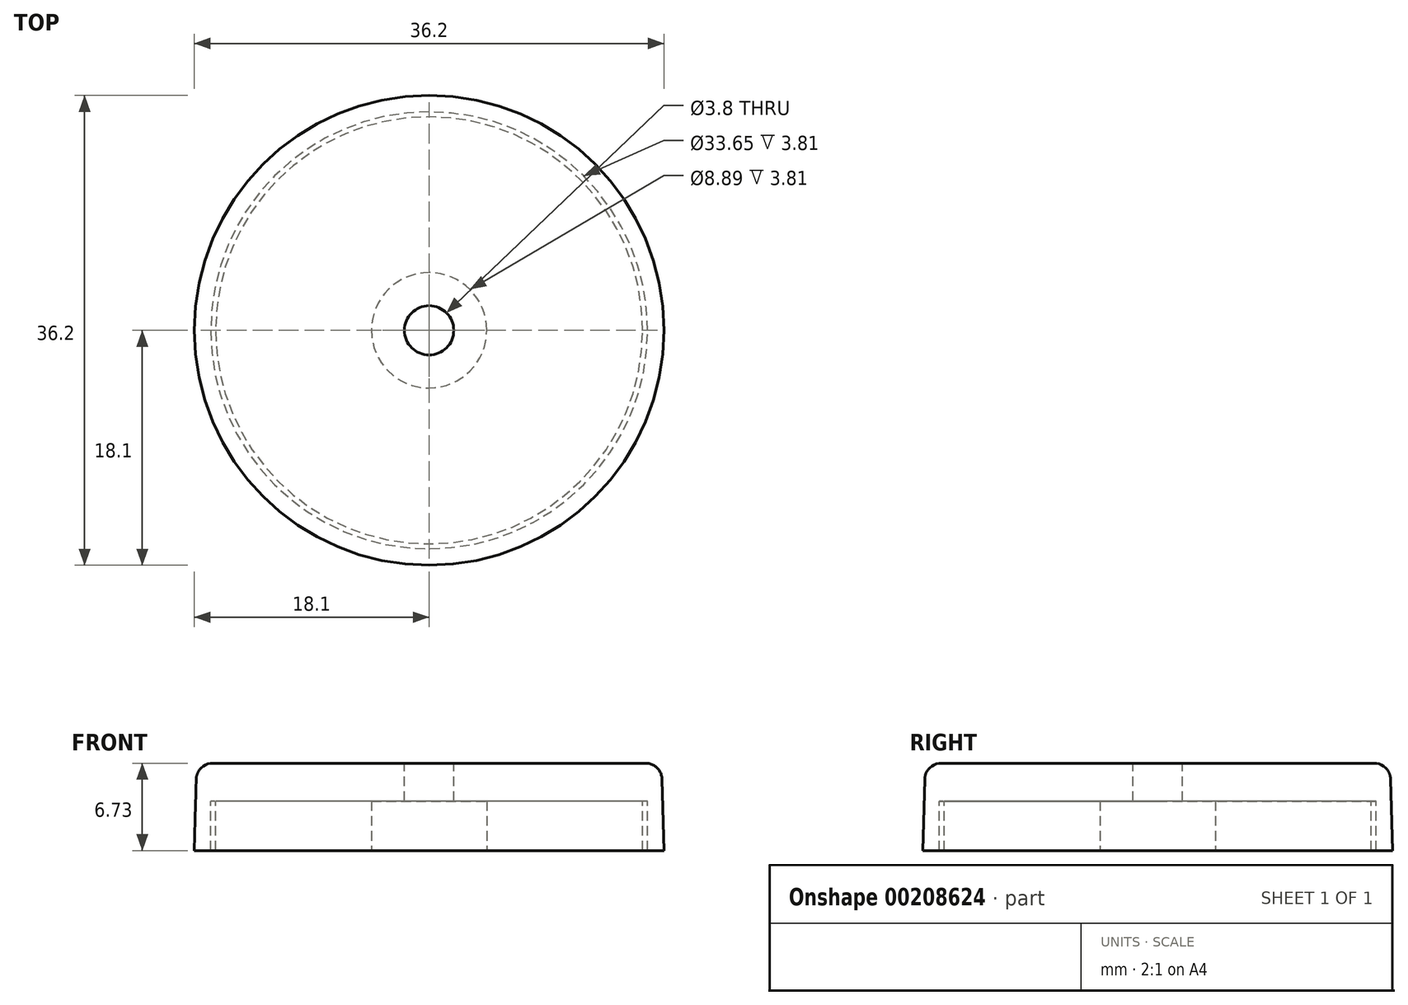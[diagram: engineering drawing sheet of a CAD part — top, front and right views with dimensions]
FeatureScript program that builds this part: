
annotation { "Feature Type Name" : "Feature", "Feature Type Description" : "" }
export const myFeature = defineFeature(function(context is Context, id is Id, definition is map)
    precondition{}
    {
        {
            var Q0;
            Q0=qCreatedBy(makeId("Front.planeOp"),FACE);
            var sketch = newSketch(context, id + "F0", { "sketchPlane" : qUnion([Q0])});
            skLineSegment(sketch, "E0.bottom", {"start": v(0, 6.73) * mm, "end": v(18.1, 6.73) * mm});
            skLineSegment(sketch, "E0.top", {"start": v(0, 0) * mm, "end": v(18.1, 0) * mm});
            skLineSegment(sketch, "E0.left", {"start": v(0, 6.73) * mm, "end": v(0, 0) * mm});
            skLineSegment(sketch, "E0.right", {"start": v(18.1, 6.73) * mm, "end": v(18.1, 0) * mm});
            skLineSegment(sketch, "E1", {"start": v(18.1, 0) * mm, "end": v(17.91, 6.73) * mm});
            skLineSegment(sketch, "E2.bottom", {"start": v(16.83, 0) * mm, "end": v(16.45, 0) * mm});
            skLineSegment(sketch, "E2.top", {"start": v(16.83, 3.8) * mm, "end": v(16.45, 3.8) * mm});
            skLineSegment(sketch, "E2.left", {"start": v(16.83, 0) * mm, "end": v(16.83, 3.81) * mm});
            skLineSegment(sketch, "E2.right", {"start": v(16.45, 0) * mm, "end": v(16.45, 3.81) * mm});
            skSolve(sketch);
        }
        {
            var Q0;
            Q0=makeQuery(id+"F0.imprint","IMPRINT",FACE,{"disambiguationData":[TD([[makeQuery(id+"F0.imprint","IMPRINT",EDGE,{"derivedFrom":sQuery(id+"F0.wireOp",EDGE,"E0.top")}),1.0]])]});
            var Q1;
            Q1=sQuery(id+"F0.wireOp",EDGE,"E0.left");
            revolve(context, id + "F1", {"entities" : qUnion([Q0]), "axis" : qUnion([Q1]), "revolveType" : RevolveType.FULL});
        }
        {
            var Q0;
            Q0=makeQuery(id+"F1.opRevolve","SWEPT_FACE",FACE,{"disambiguationData":[OSD([sQuery(id+"F0.wireOp",EDGE,"E0.bottom")])]});
            var sketch = newSketch(context, id + "F2", { "sketchPlane" : qUnion([Q0])});
            skPoint(sketch, "E3", {"position": v(0, 0) * mm});
            skSolve(sketch);
        }
        {
            var Q0;
            Q0=sQuery(id+"F2.wireOp",VERTEX,"E3");
            var Q1;
            Q1=makeQuery(id+"F1.opRevolve","SWEPT_BODY",BODY,{"disambiguationData":[OSD([sQuery(id+"F0.wireOp",EDGE,"E0.bottom"),sQuery(id+"F0.wireOp",EDGE,"E0.top"),sQuery(id+"F0.wireOp",EDGE,"E0.left"),sQuery(id+"F0.wireOp",EDGE,"E1")])]});
            hole(context, id + "F3", {"style" : HoleStyle.SIMPLE, "endStyle" : HoleEndStyle.THROUGH, "standardTappedOrClearance" : lookupTablePath({ "standard" : "ANSI", "fit" : "Normal (ASME)", "size" : "#6", "type" : "Clearance" }), "standardBlindInLast" : lookupTablePath({ "fit" : "Free", "standard" : "ANSI", "size" : "#6", "type" : "Clearance" }), "holeDiameter" : 3.8 * mm, "locations" : qUnion([Q0]), "scope" : qUnion([Q1]), "isTappedThrough" : true});
        }
        {
            var Q0;
            {var subQ0=sQuery(id+"F0.wireOp",EDGE,"E0.top");Q0=makeQuery(id+"F1.opRevolve","SWEPT_FACE",FACE,{"disambiguationData":[OSD([subQ0]),TDD([makeQuery(id+"F0.imprint","IMPRINT",EDGE,{"disambiguationData":[TD([[makeQuery(id+"F0.imprint","INTERSECT",VERTEX,{"derivedFrom":[subQ0,sQuery(id+"F0.wireOp",EDGE,"E0.left")]}),-1.0]])],"derivedFrom":subQ0})])]});}
            var sketch = newSketch(context, id + "F4", { "sketchPlane" : qUnion([Q0])});
            skCircle(sketch, "E4", {"center": v(0, 0) * mm, "radius": 4.45 * mm});
            skSolve(sketch);
        }
        {
            var Q0;
            Q0=makeQuery(id+"F4.imprint","IMPRINT",FACE,{"disambiguationData":[TD([[makeQuery(id+"F4.imprint","IMPRINT",EDGE,{"derivedFrom":sQuery(id+"F4.wireOp",EDGE,"E4")}),1.0]])]});
            extrude(context, id + "F5", {"entities" : qUnion([Q0]), "operationType" : NewBodyOperationType.REMOVE, "oppositeDirection" : true, "depth" : 3.8 * mm});
        }
        {
            var Q0;
            Q0=makeQuery(id+"F1.opRevolve","SWEPT_EDGE",EDGE,{"disambiguationData":[OSD([sQuery(id+"F0.wireOp",EDGE,"E0.bottom"),sQuery(id+"F0.wireOp",EDGE,"E1")])]});
            fillet(context, id + "F6", {"entities" : qUnion([Q0]), "radius" : 1.27 * mm, "tangentPropagation" : true, "allowEdgeOverflow" : false});
        }
    });
